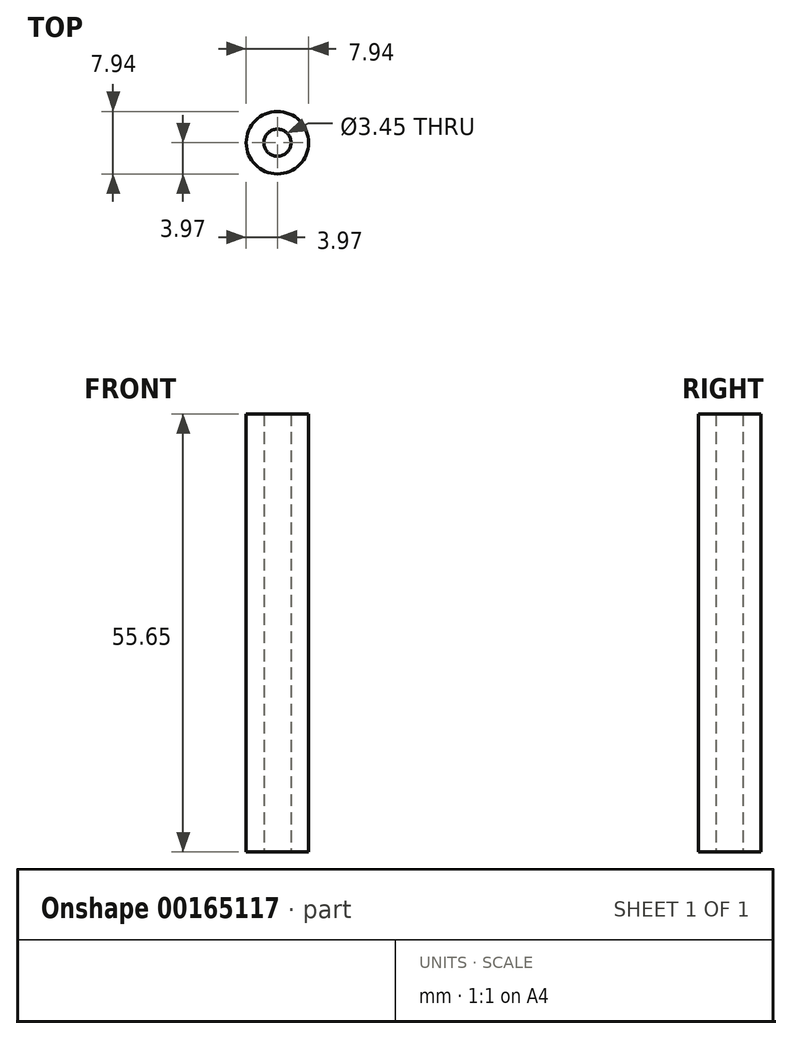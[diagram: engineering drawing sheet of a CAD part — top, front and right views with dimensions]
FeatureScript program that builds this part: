
annotation { "Feature Type Name" : "Feature", "Feature Type Description" : "" }
export const myFeature = defineFeature(function(context is Context, id is Id, definition is map)
    precondition{}
    {
        {
            var Q0;
            Q0=qCreatedBy(makeId("Top.planeOp"),FACE);
            var sketch = newSketch(context, id + "F0", { "sketchPlane" : qUnion([Q0])});
            skCircle(sketch, "E0", {"center": v(0, 0) * mm, "radius": 1.73 * mm});
            skCircle(sketch, "E1", {"center": v(0, 0) * mm, "radius": 3.97 * mm});
            skSolve(sketch);
        }
        {
            var Q0;
            Q0 = qSketchRegion(id + "F0", true);
            extrude(context, id + "F1", {"entities" : qUnion([Q0]), "depth" : 55.65 * mm});
        }
    });
